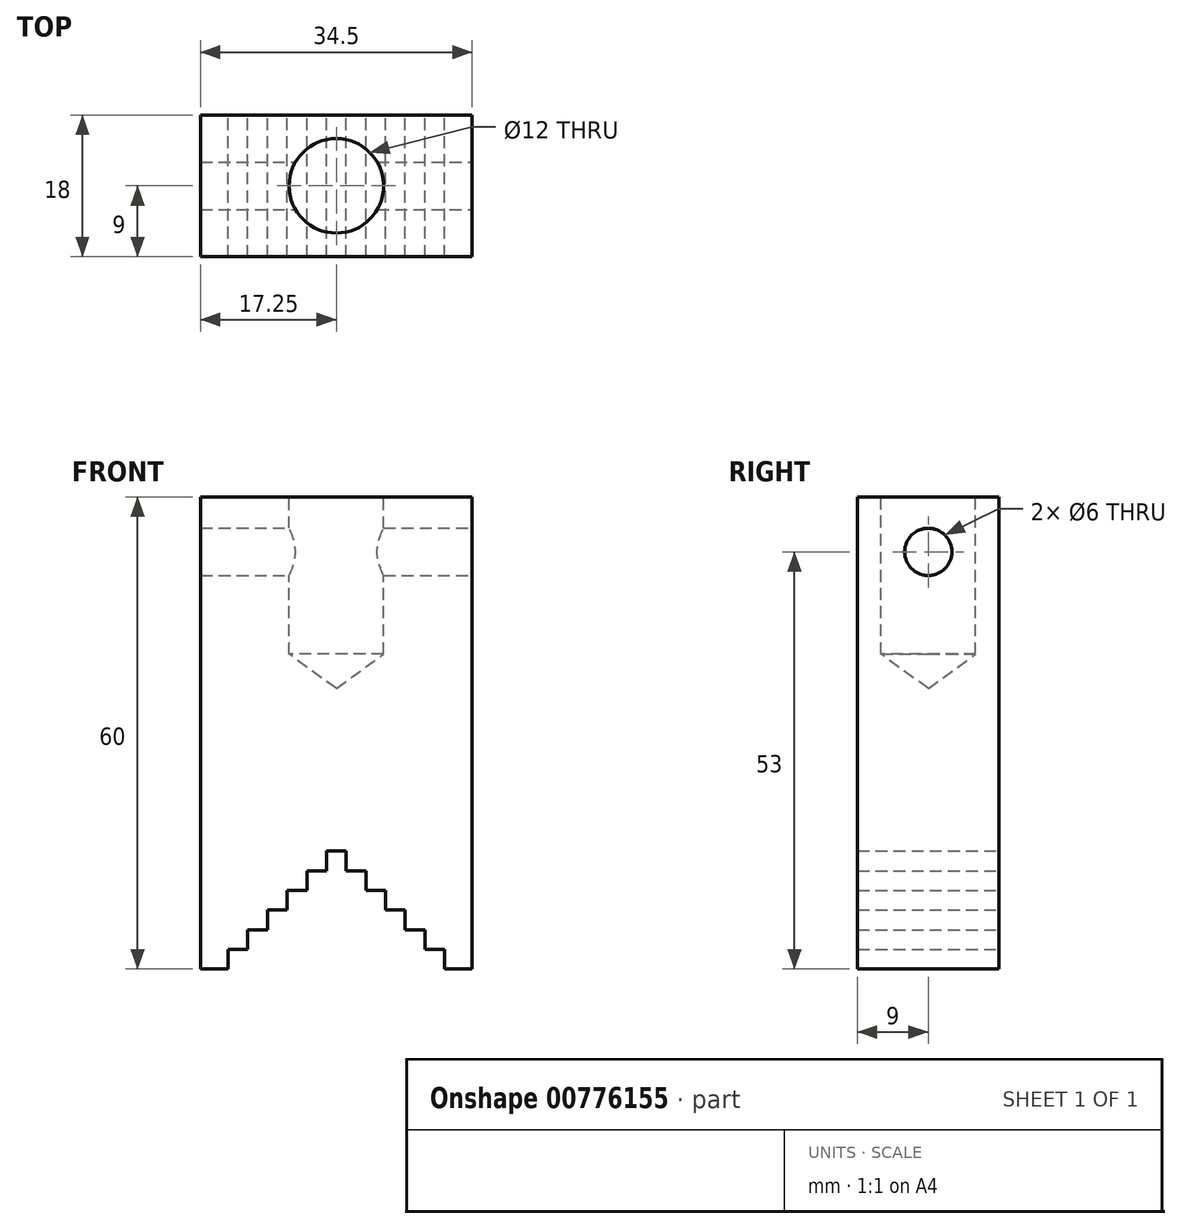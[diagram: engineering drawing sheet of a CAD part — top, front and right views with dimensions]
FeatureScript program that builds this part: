
annotation { "Feature Type Name" : "Feature", "Feature Type Description" : "" }
export const myFeature = defineFeature(function(context is Context, id is Id, definition is map)
    precondition{}
    {
        {
            var Q0;
            Q0=qCreatedBy(makeId("Front.planeOp"),FACE);
            var sketch = newSketch(context, id + "F0", { "sketchPlane" : qUnion([Q0])});
            skLineSegment(sketch, "E0.bottom", {"start": v(17.25, 30) * mm, "end": v(-17.25, 30) * mm});
            skLineSegment(sketch, "E0.left", {"start": v(17.25, 30) * mm, "end": v(17.25, -30) * mm});
            skLineSegment(sketch, "E0.right", {"start": v(-17.25, 30) * mm, "end": v(-17.25, -30) * mm});
            skPoint(sketch, "E0.middle", {"position": v(0, 0) * mm});
            skLineSegment(sketch, "E1", {"start": v(-17.25, -30) * mm, "end": v(-13.75, -30) * mm});
            skLineSegment(sketch, "E2", {"start": v(-13.75, -30) * mm, "end": v(-13.75, -27.5) * mm});
            skLineSegment(sketch, "E3", {"start": v(-13.75, -27.5) * mm, "end": v(-11.25, -27.5) * mm});
            skLineSegment(sketch, "E4", {"start": v(-11.25, -27.5) * mm, "end": v(-11.25, -25) * mm});
            skLineSegment(sketch, "E5", {"start": v(-11.25, -25) * mm, "end": v(-8.75, -25) * mm});
            skLineSegment(sketch, "E6", {"start": v(-8.75, -25) * mm, "end": v(-8.75, -22.5) * mm});
            skLineSegment(sketch, "E7", {"start": v(-8.75, -22.5) * mm, "end": v(-6.25, -22.5) * mm});
            skLineSegment(sketch, "E8", {"start": v(-6.25, -22.5) * mm, "end": v(-6.25, -20) * mm});
            skLineSegment(sketch, "E9", {"start": v(-6.25, -20) * mm, "end": v(-3.75, -20) * mm});
            skLineSegment(sketch, "E10", {"start": v(-3.75, -20) * mm, "end": v(-3.75, -17.5) * mm});
            skLineSegment(sketch, "E11", {"start": v(-3.75, -17.5) * mm, "end": v(-1.25, -17.5) * mm});
            skLineSegment(sketch, "E12", {"start": v(-1.25, -15) * mm, "end": v(1.25, -15) * mm});
            skLineSegment(sketch, "E13", {"start": v(1.25, -15) * mm, "end": v(1.25, -17.5) * mm});
            skLineSegment(sketch, "E14", {"start": v(-1.25, -15) * mm, "end": v(-1.25, -17.5) * mm});
            skLineSegment(sketch, "E15", {"start": v(1.25, -17.5) * mm, "end": v(3.75, -17.5) * mm});
            skLineSegment(sketch, "E16", {"start": v(3.75, -17.5) * mm, "end": v(3.75, -20) * mm});
            skLineSegment(sketch, "E17", {"start": v(3.75, -20) * mm, "end": v(6.25, -20) * mm});
            skLineSegment(sketch, "E18", {"start": v(6.25, -20) * mm, "end": v(6.25, -22.5) * mm});
            skLineSegment(sketch, "E19", {"start": v(6.25, -22.5) * mm, "end": v(8.75, -22.5) * mm});
            skLineSegment(sketch, "E20", {"start": v(8.75, -22.5) * mm, "end": v(8.75, -25) * mm});
            skLineSegment(sketch, "E21", {"start": v(8.75, -25) * mm, "end": v(11.25, -25) * mm});
            skLineSegment(sketch, "E22", {"start": v(11.25, -25) * mm, "end": v(11.25, -27.5) * mm});
            skLineSegment(sketch, "E23", {"start": v(11.25, -27.5) * mm, "end": v(13.75, -27.5) * mm});
            skLineSegment(sketch, "E24", {"start": v(13.75, -27.5) * mm, "end": v(13.75, -30) * mm});
            skLineSegment(sketch, "E25", {"start": v(13.75, -30) * mm, "end": v(17.25, -30) * mm});
            skLineSegment(sketch, "E26", {"start": v(17.25, -30) * mm, "end": v(-17.25, -30) * mm, "construction": true});
            skLineSegment(sketch, "E27", {"start": v(0, -30) * mm, "end": v(0, 0) * mm, "construction": true});
            skLineSegment(sketch, "E28", {"start": v(0, 30) * mm, "end": v(0, 0) * mm, "construction": true});
            skSolve(sketch);
        }
        {
            var Q0;
            Q0 = qSketchRegion(id + "F0", true);
            extrude(context, id + "F1", {"entities" : qUnion([Q0]), "depth" : 18 * mm, "offsetDistance" : 25 * mm, "symmetric" : true});
        }
        {
            var Q0;
            Q0=makeQuery(id+"F1.opExtrude","SWEPT_FACE",FACE,{"disambiguationData":[OSD([sQuery(id+"F0.wireOp",EDGE,"E0.left")])]});
            var sketch = newSketch(context, id + "F2", { "sketchPlane" : qUnion([Q0])});
            skCircle(sketch, "E29", {"center": v(0, 23) * mm, "radius": 3 * mm});
            skSolve(sketch);
        }
        {
            var Q0;
            Q0 = qSketchRegion(id + "F2", true);
            extrude(context, id + "F3", {"entities" : qUnion([Q0]), "operationType" : NewBodyOperationType.REMOVE, "oppositeDirection" : true, "depth" : 35 * mm, "offsetDistance" : 25 * mm});
        }
        {
            var Q0;
            Q0=makeQuery(id+"F1.opExtrude","CAP_FACE",FACE,{"disambiguationData":[OSD([sQuery(id+"F0.wireOp",EDGE,"E0.bottom"),sQuery(id+"F0.wireOp",EDGE,"E0.left"),sQuery(id+"F0.wireOp",EDGE,"E0.right"),sQuery(id+"F0.wireOp",EDGE,"E1"),sQuery(id+"F0.wireOp",EDGE,"E2"),sQuery(id+"F0.wireOp",EDGE,"E3"),sQuery(id+"F0.wireOp",EDGE,"E4"),sQuery(id+"F0.wireOp",EDGE,"E5"),sQuery(id+"F0.wireOp",EDGE,"E6"),sQuery(id+"F0.wireOp",EDGE,"E7"),sQuery(id+"F0.wireOp",EDGE,"E8"),sQuery(id+"F0.wireOp",EDGE,"E9"),sQuery(id+"F0.wireOp",EDGE,"E10"),sQuery(id+"F0.wireOp",EDGE,"E11"),sQuery(id+"F0.wireOp",EDGE,"E12"),sQuery(id+"F0.wireOp",EDGE,"E13"),sQuery(id+"F0.wireOp",EDGE,"E14"),sQuery(id+"F0.wireOp",EDGE,"E15"),sQuery(id+"F0.wireOp",EDGE,"E16"),sQuery(id+"F0.wireOp",EDGE,"E17"),sQuery(id+"F0.wireOp",EDGE,"E18"),sQuery(id+"F0.wireOp",EDGE,"E19"),sQuery(id+"F0.wireOp",EDGE,"E20"),sQuery(id+"F0.wireOp",EDGE,"E21"),sQuery(id+"F0.wireOp",EDGE,"E22"),sQuery(id+"F0.wireOp",EDGE,"E23"),sQuery(id+"F0.wireOp",EDGE,"E24"),sQuery(id+"F0.wireOp",EDGE,"E25")])],"isStart":false});
            var Q1;
            Q1=makeQuery(id+"F1.opExtrude","CAP_FACE",FACE,{"disambiguationData":[OSD([sQuery(id+"F0.wireOp",EDGE,"E0.bottom"),sQuery(id+"F0.wireOp",EDGE,"E0.left"),sQuery(id+"F0.wireOp",EDGE,"E0.right"),sQuery(id+"F0.wireOp",EDGE,"E1"),sQuery(id+"F0.wireOp",EDGE,"E2"),sQuery(id+"F0.wireOp",EDGE,"E3"),sQuery(id+"F0.wireOp",EDGE,"E4"),sQuery(id+"F0.wireOp",EDGE,"E5"),sQuery(id+"F0.wireOp",EDGE,"E6"),sQuery(id+"F0.wireOp",EDGE,"E7"),sQuery(id+"F0.wireOp",EDGE,"E8"),sQuery(id+"F0.wireOp",EDGE,"E9"),sQuery(id+"F0.wireOp",EDGE,"E10"),sQuery(id+"F0.wireOp",EDGE,"E11"),sQuery(id+"F0.wireOp",EDGE,"E12"),sQuery(id+"F0.wireOp",EDGE,"E13"),sQuery(id+"F0.wireOp",EDGE,"E14"),sQuery(id+"F0.wireOp",EDGE,"E15"),sQuery(id+"F0.wireOp",EDGE,"E16"),sQuery(id+"F0.wireOp",EDGE,"E17"),sQuery(id+"F0.wireOp",EDGE,"E18"),sQuery(id+"F0.wireOp",EDGE,"E19"),sQuery(id+"F0.wireOp",EDGE,"E20"),sQuery(id+"F0.wireOp",EDGE,"E21"),sQuery(id+"F0.wireOp",EDGE,"E22"),sQuery(id+"F0.wireOp",EDGE,"E23"),sQuery(id+"F0.wireOp",EDGE,"E24"),sQuery(id+"F0.wireOp",EDGE,"E25")])],"isStart":true});
            cPlane(context, id + "F4", {"entities" : qUnion([Q0, Q1]), "cplaneType" : CPlaneType.MID_PLANE, "offset" : 25 * mm, "width" : 150 * mm, "height" : 150 * mm});
        }
        {
            var Q0;
            Q0=qCreatedBy(id+"F4.planeOp",FACE);
            var sketch = newSketch(context, id + "F5", { "sketchPlane" : qUnion([Q0])});
            skLineSegment(sketch, "E30", {"start": v(-6, 30) * mm, "end": v(6, 30) * mm});
            skLineSegment(sketch, "E31", {"start": v(6, 30) * mm, "end": v(6, 10) * mm});
            skLineSegment(sketch, "E32", {"start": v(6, 10) * mm, "end": v(0, 5.64) * mm});
            skLineSegment(sketch, "E33", {"start": v(0, 5.64) * mm, "end": v(-6, 10) * mm});
            skLineSegment(sketch, "E34", {"start": v(-6, 10) * mm, "end": v(-6, 30) * mm});
            skLineSegment(sketch, "E35", {"start": v(0, 5.64) * mm, "end": v(0, 30) * mm});
            skSolve(sketch);
        }
        {
            var Q0;
            Q0=makeQuery(id+"F5.imprint","IMPRINT",FACE,{"disambiguationData":[TD([[makeQuery(id+"F5.imprint","IMPRINT",EDGE,{"derivedFrom":sQuery(id+"F5.wireOp",EDGE,"E33")}),-1.0]])]});
            var Q1;
            Q1=sQuery(id+"F5.wireOp",EDGE,"E35");
            revolve(context, id + "F6", {"operationType" : NewBodyOperationType.REMOVE, "surfaceOperationType" : NewSurfaceOperationType.NEW, "entities" : qUnion([Q0]), "axis" : qUnion([Q1]), "revolveType" : RevolveType.FULL, "oppositeDirection" : true});
        }
    });
